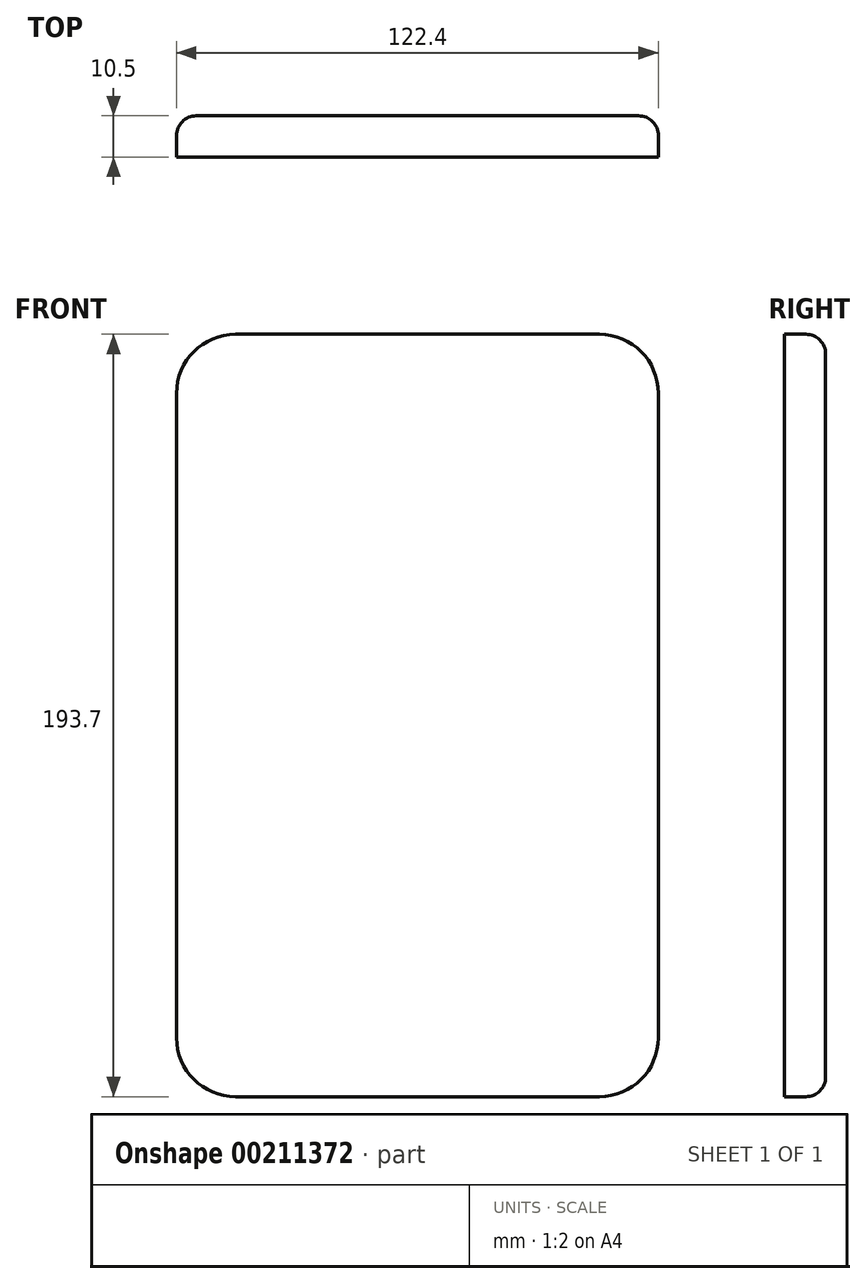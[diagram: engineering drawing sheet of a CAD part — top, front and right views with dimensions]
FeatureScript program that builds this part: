
annotation { "Feature Type Name" : "Feature", "Feature Type Description" : "" }
export const myFeature = defineFeature(function(context is Context, id is Id, definition is map)
    precondition{}
    {
        {
            var Q0;
            Q0=qCreatedBy(makeId("Front.planeOp"),FACE);
            var sketch = newSketch(context, id + "F0", { "sketchPlane" : qUnion([Q0])});
            skLineSegment(sketch, "E0.bottom", {"start": v(61.2, 96.85) * mm, "end": v(-61.2, 96.85) * mm});
            skLineSegment(sketch, "E0.top", {"start": v(61.2, -96.85) * mm, "end": v(-61.2, -96.85) * mm});
            skLineSegment(sketch, "E0.left", {"start": v(61.2, 96.85) * mm, "end": v(61.2, -96.85) * mm});
            skLineSegment(sketch, "E0.right", {"start": v(-61.2, 96.85) * mm, "end": v(-61.2, -96.85) * mm});
            skPoint(sketch, "E0.middle", {"position": v(0, 0) * mm});
            skSolve(sketch);
        }
        {
            var Q0;
            Q0=makeQuery(id+"F0.imprint","IMPRINT",FACE,{"disambiguationData":[TD([[makeQuery(id+"F0.imprint","IMPRINT",EDGE,{"derivedFrom":sQuery(id+"F0.wireOp",EDGE,"E0.bottom")}),1.0]])]});
            extrude(context, id + "F1", {"entities" : qUnion([Q0]), "depth" : 10.5 * mm});
        }
        {
            var Q0;
            Q0=makeQuery(id+"F1.opExtrude","SWEPT_EDGE",EDGE,{"disambiguationData":[OSD([sQuery(id+"F0.wireOp",EDGE,"E0.bottom"),sQuery(id+"F0.wireOp",EDGE,"E0.left")])]});
            var Q1;
            Q1=makeQuery(id+"F1.opExtrude","SWEPT_EDGE",EDGE,{"disambiguationData":[OSD([sQuery(id+"F0.wireOp",EDGE,"E0.top"),sQuery(id+"F0.wireOp",EDGE,"E0.left")])]});
            var Q2;
            Q2=makeQuery(id+"F1.opExtrude","SWEPT_EDGE",EDGE,{"disambiguationData":[OSD([sQuery(id+"F0.wireOp",EDGE,"E0.bottom"),sQuery(id+"F0.wireOp",EDGE,"E0.right")])]});
            var Q3;
            Q3=makeQuery(id+"F1.opExtrude","SWEPT_EDGE",EDGE,{"disambiguationData":[OSD([sQuery(id+"F0.wireOp",EDGE,"E0.top"),sQuery(id+"F0.wireOp",EDGE,"E0.right")])]});
            fillet(context, id + "F2", {"entities" : qUnion([Q0, Q1, Q2, Q3]), "radius" : 15 * mm, "tangentPropagation" : true, "allowEdgeOverflow" : false});
        }
        {
            var Q0;
            Q0=makeQuery(id+"F1.opExtrude","CAP_EDGE",EDGE,{"disambiguationData":[OSD([sQuery(id+"F0.wireOp",EDGE,"E0.left")])],"isStart":true});
            fillet(context, id + "F3", {"entities" : qUnion([Q0]), "radius" : 5 * mm, "tangentPropagation" : true, "allowEdgeOverflow" : false});
        }
    });
